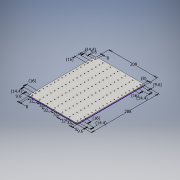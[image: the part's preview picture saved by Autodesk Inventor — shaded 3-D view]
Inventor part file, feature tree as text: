
AUTODESK INVENTOR PART (.ipt)
format: ipt  version: 2016 (Build 200138000, 138)  size: 274,432 bytes
history: native  units: mm
features: reference x112, extrude x1, sketch x1
ambient origin geometry x8: Origin, YZ Plane, XZ Plane, XY Plane, X Axis, Y Axis, Z Axis, Center Point
bodies: Body1 (feature_tree)
feature tree (114):
  extrude  "Extrusion8"  Depth=4.0mm
  sketch  "Sketch1"  dims[d0=208.0mm d1=288.0mm d17=32.0mm d18=32.0mm d19=32.0mm d20=32.0mm d21=32.0mm d22=32.0mm d23=8.0mm d25=9.6mm d26=9.6mm d27=8.0mm d29=9.6mm d30=8.0mm d31=14.4mm d32=16.0mm d33=14.4mm d34=14.4mm d35=16.0mm d36=14.4mm d37=16.0mm d38=16.0mm d39=9.6mm d40=8.0mm d41=4.0mm d42=0.0mm]
  reference  "Reference4"
  reference  "Reference8"
  reference  "Reference9"
  reference  "Reference10"
  reference  "Reference11"
  reference  "Reference12"
  reference  "Reference13"
  reference  "Reference14"
  reference  "Reference15"
  reference  "Reference16"
  reference  "Reference17"
  reference  "Reference18"
  reference  "Reference19"
  reference  "Reference20"
  reference  "Reference21"
  reference  "Reference22"
  reference  "Reference23"
  reference  "Reference24"
  reference  "Reference25"
  reference  "Reference26"
  reference  "Reference27"
  reference  "Reference28"
  reference  "Reference29"
  reference  "Reference30"
  reference  "Reference31"
  reference  "Reference32"
  reference  "Reference33"
  reference  "Reference34"
  reference  "Reference35"
  reference  "Reference36"
  reference  "Reference37"
  reference  "Reference38"
  reference  "Reference39"
  reference  "Reference40"
  reference  "Reference41"
  reference  "Reference42"
  reference  "Reference43"
  reference  "Reference44"
  reference  "Reference45"
  reference  "Reference46"
  reference  "Reference47"
  reference  "Reference48"
  reference  "Reference49"
  reference  "Reference50"
  reference  "Reference51"
  reference  "Reference52"
  reference  "Reference53"
  reference  "Reference54"
  reference  "Reference55"
  reference  "Reference56"
  reference  "Reference57"
  reference  "Reference58"
  reference  "Reference59"
  reference  "Reference60"
  reference  "Reference61"
  reference  "Reference62"
  reference  "Reference63"
  reference  "Reference64"
  reference  "Reference65"
  reference  "Reference66"
  reference  "Reference67"
  reference  "Reference68"
  reference  "Reference69"
  reference  "Reference70"
  reference  "Reference71"
  reference  "Reference72"
  reference  "Reference73"
  reference  "Reference74"
  reference  "Reference75"
  reference  "Reference76"
  reference  "Reference77"
  reference  "Reference78"
  reference  "Reference79"
  reference  "Reference80"
  reference  "Reference81"
  reference  "Reference82"
  reference  "Reference83"
  reference  "Reference84"
  reference  "Reference85"
  reference  "Reference86"
  reference  "Reference87"
  reference  "Reference88"
  reference  "Reference89"
  reference  "Reference90"
  reference  "Reference91"
  reference  "Reference92"
  reference  "Reference93"
  reference  "Reference94"
  reference  "Reference95"
  reference  "Reference96"
  reference  "Reference97"
  reference  "Reference98"
  reference  "Reference99"
  reference  "Reference100"
  reference  "Reference101"
  reference  "Reference102"
  reference  "Reference103"
  reference  "Reference104"
  reference  "Reference105"
  reference  "Reference106"
  reference  "Reference107"
  reference  "Reference108"
  reference  "Reference109"
  reference  "Reference110"
  reference  "Reference111"
  reference  "Reference112"
  reference  "Reference113"
  reference  "Reference114"
  reference  "Reference115"
  reference  "Reference116"
  reference  "Reference117"
  reference  "Reference118"
